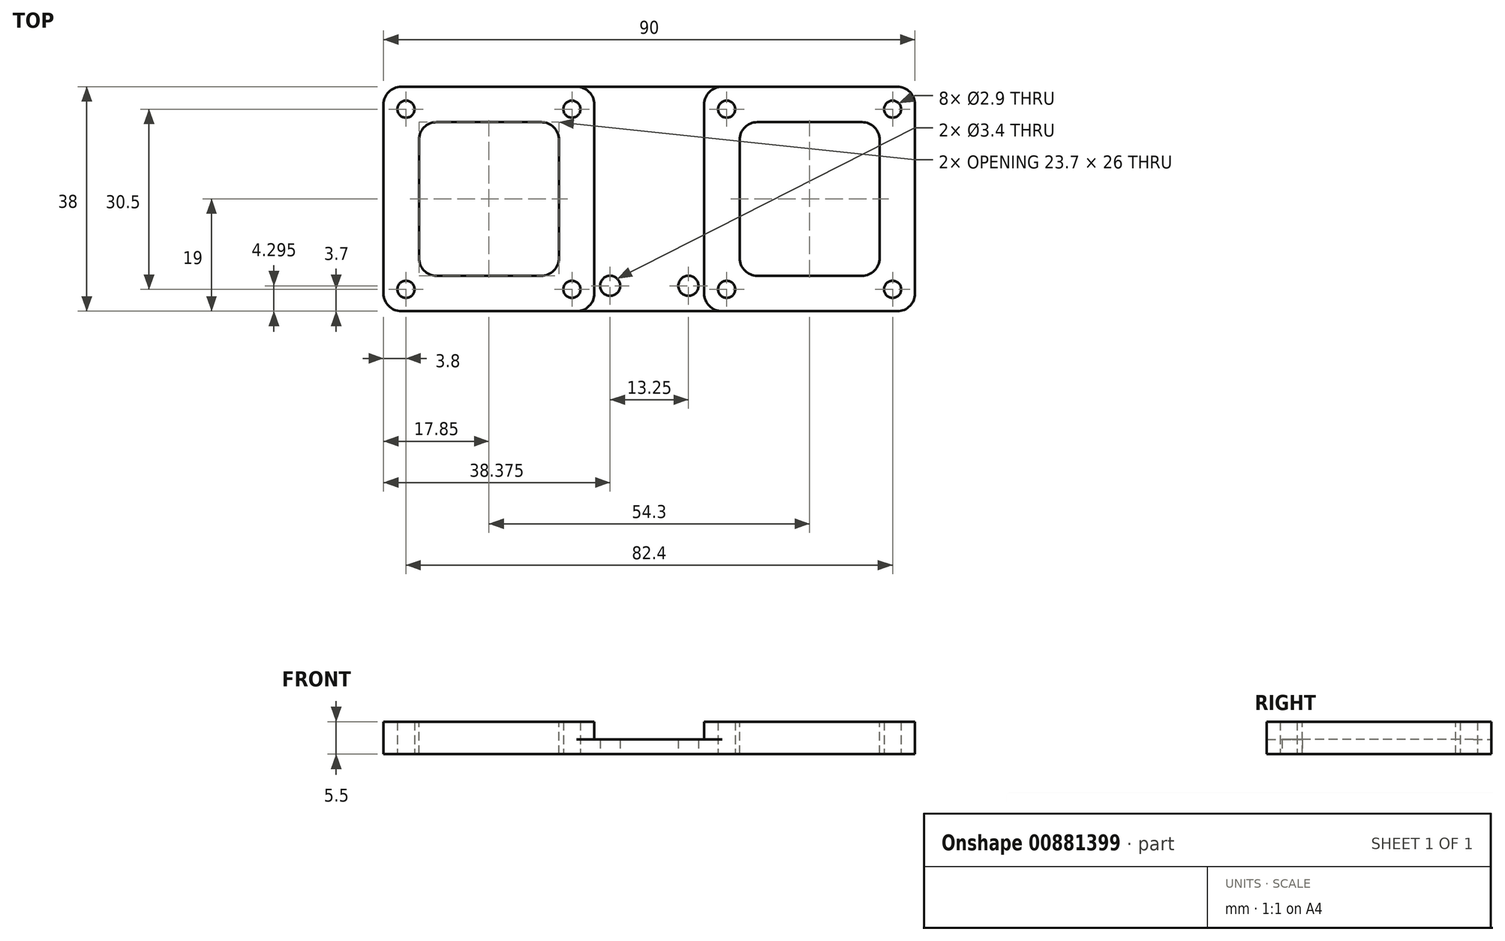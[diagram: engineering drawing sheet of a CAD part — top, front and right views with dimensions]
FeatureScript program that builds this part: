
annotation { "Feature Type Name" : "Feature", "Feature Type Description" : "" }
export const myFeature = defineFeature(function(context is Context, id is Id, definition is map)
    precondition{}
    {
        {
            var Q0;
            Q0=qCreatedBy(makeId("Top.planeOp"),FACE);
            var sketch = newSketch(context, id + "F0", { "sketchPlane" : qUnion([Q0])});
            skLineSegment(sketch, "E0.bottom", {"start": v(45, -19) * mm, "end": v(-45, -19) * mm});
            skLineSegment(sketch, "E0.top", {"start": v(45, 19) * mm, "end": v(-45, 19) * mm});
            skLineSegment(sketch, "E0.left", {"start": v(45, -19) * mm, "end": v(45, 19) * mm});
            skLineSegment(sketch, "E0.right", {"start": v(-45, -19) * mm, "end": v(-45, 19) * mm});
            skPoint(sketch, "E0.middle", {"position": v(0, 0) * mm});
            skSolve(sketch);
        }
        {
            var Q0;
            Q0=makeQuery(id+"F0.imprint","IMPRINT",FACE,{"disambiguationData":[TD([[makeQuery(id+"F0.imprint","IMPRINT",EDGE,{"derivedFrom":sQuery(id+"F0.wireOp",EDGE,"E0.bottom")}),-1.0]])]});
            extrude(context, id + "F1", {"entities" : qUnion([Q0]), "depth" : 2.5 * mm, "offsetDistance" : 25 * mm});
        }
        {
            var Q0;
            Q0=makeQuery(id+"F1.opExtrude","CAP_FACE",FACE,{"disambiguationData":[OSD([sQuery(id+"F0.wireOp",EDGE,"E0.bottom"),sQuery(id+"F0.wireOp",EDGE,"E0.top"),sQuery(id+"F0.wireOp",EDGE,"E0.left"),sQuery(id+"F0.wireOp",EDGE,"E0.right")])],"isStart":false});
            var sketch = newSketch(context, id + "F2", { "sketchPlane" : qUnion([Q0])});
            skPoint(sketch, "E1", {"position": v(-9.3, 19) * mm});
            skPoint(sketch, "E2", {"position": v(-9.3, -19) * mm});
            skPoint(sketch, "E3", {"position": v(9.3, 19) * mm});
            skPoint(sketch, "E4", {"position": v(9.3, -19) * mm});
            skLineSegment(sketch, "E5", {"start": v(-9.3, 19) * mm, "end": v(-9.3, -19) * mm});
            skLineSegment(sketch, "E6", {"start": v(9.3, 19) * mm, "end": v(9.3, -19) * mm});
            skPoint(sketch, "E7", {"position": v(6.62, -14.7) * mm});
            skPoint(sketch, "E8", {"position": v(-6.62, -14.7) * mm});
            skPoint(sketch, "E9", {"position": v(0, -14.7) * mm});
            skSolve(sketch);
        }
        {
            var Q0;
            Q0=sQuery(id+"F2.wireOp",VERTEX,"E7");
            var Q1;
            Q1=sQuery(id+"F2.wireOp",VERTEX,"E8");
            var Q2;
            Q2=makeQuery(id+"F1.opExtrude","SWEPT_BODY",BODY,{"disambiguationData":[OSD([sQuery(id+"F0.wireOp",EDGE,"E0.bottom"),sQuery(id+"F0.wireOp",EDGE,"E0.top"),sQuery(id+"F0.wireOp",EDGE,"E0.left"),sQuery(id+"F0.wireOp",EDGE,"E0.right")])]});
            hole(context, id + "F3", {"style" : HoleStyle.SIMPLE, "endStyle" : HoleEndStyle.THROUGH, "standardTappedOrClearance" : lookupTablePath({ "fit" : "Normal", "standard" : "ISO", "size" : "M3", "type" : "Clearance" }), "standardBlindInLast" : lookupTablePath({ "fit" : "Normal", "standard" : "ISO", "engagement" : "75%", "pitch" : "0.5 mm", "size" : "M3", "type" : "Clearance & tapped" }), "holeDiameter" : 3.4 * mm, "majorDiameter" : 5 * mm, "isTappedThrough" : true, "tappedDepth" : 12 * mm, "tapClearance" : 3, "locations" : qUnion([Q0, Q1]), "scope" : qUnion([Q2]), "startStyle" : HoleStartStyle.SKETCH});
        }
        {
            var Q0;
            {var subQ0=sQuery(id+"F2.wireOp",EDGE,"E5");Q0=makeQuery(id+"F2.imprint","IMPRINT",FACE,{"disambiguationData":[TD([[makeQuery(id+"F2.imprint","IMPRINT",EDGE,{"derivedFrom":subQ0}),-1.0]])]});}
            var Q1;
            {var subQ0=sQuery(id+"F2.wireOp",EDGE,"E6");Q1=makeQuery(id+"F2.imprint","IMPRINT",FACE,{"disambiguationData":[TD([[makeQuery(id+"F2.imprint","IMPRINT",EDGE,{"derivedFrom":subQ0}),1.0]])]});}
            extrude(context, id + "F4", {"entities" : qUnion([Q0, Q1]), "operationType" : NewBodyOperationType.ADD, "depth" : 3 * mm, "offsetDistance" : 25 * mm});
        }
        {
            var Q0;
            Q0=makeQuery(id+"F4.opExtrude","CAP_FACE",FACE,{"disambiguationData":[OSD([sQuery(id+"F0.wireOp",EDGE,"E0.bottom"),sQuery(id+"F0.wireOp",EDGE,"E0.top"),sQuery(id+"F0.wireOp",EDGE,"E0.right"),sQuery(id+"F2.wireOp",EDGE,"E5")])],"isStart":false});
            var sketch = newSketch(context, id + "F5", { "sketchPlane" : qUnion([Q0])});
            skLineSegment(sketch, "E10.0", {"start": v(39, 13) * mm, "end": v(15.3, 13) * mm});
            skLineSegment(sketch, "E10.1", {"start": v(39, -13) * mm, "end": v(39, 13) * mm});
            skLineSegment(sketch, "E10.2", {"start": v(15.3, -13) * mm, "end": v(39, -13) * mm});
            skLineSegment(sketch, "E10.3", {"start": v(15.3, 13) * mm, "end": v(15.3, -13) * mm});
            skSolve(sketch);
        }
        {
            var Q0;
            {var subQ0=sQuery(id+"F2.wireOp",EDGE,"E5");Q0=makeQuery(id+"F5.imprint","IMPRINT",FACE,{"disambiguationData":[TD([[makeQuery(id+"F5.imprint","IMPRINT",EDGE,{"derivedFrom":makeQuery(id+"F4.opExtrude","CAP_EDGE",EDGE,{"disambiguationData":[OSD([subQ0])],"isStart":false})}),-1.0]])]});}
            var sketch = newSketch(context, id + "F6", { "sketchPlane" : qUnion([Q0])});
            skLineSegment(sketch, "E11.0", {"start": v(-15.3, -13) * mm, "end": v(-15.3, 13) * mm});
            skLineSegment(sketch, "E11.1", {"start": v(-39, -13) * mm, "end": v(-15.3, -13) * mm});
            skLineSegment(sketch, "E11.2", {"start": v(-39, 13) * mm, "end": v(-39, -13) * mm});
            skLineSegment(sketch, "E11.3", {"start": v(-15.3, 13) * mm, "end": v(-39, 13) * mm});
            skSolve(sketch);
        }
        {
            var Q0;
            Q0=makeQuery(id+"F6.imprint","IMPRINT",FACE,{"disambiguationData":[TD([[makeQuery(id+"F6.imprint","IMPRINT",EDGE,{"derivedFrom":sQuery(id+"F6.wireOp",EDGE,"E11.0")}),1.0]])]});
            var Q1;
            Q1=makeQuery(id+"F5.imprint","IMPRINT",FACE,{"disambiguationData":[TD([[makeQuery(id+"F5.imprint","IMPRINT",EDGE,{"derivedFrom":sQuery(id+"F5.wireOp",EDGE,"E10.0")}),1.0]])]});
            extrude(context, id + "F7", {"entities" : qUnion([Q0, Q1]), "operationType" : NewBodyOperationType.REMOVE, "oppositeDirection" : true, "depth" : 10 * mm, "offsetDistance" : 25 * mm});
        }
        {
            var Q0;
            Q0=makeQuery(id+"F4.opExtrude","CAP_FACE",FACE,{"disambiguationData":[OSD([sQuery(id+"F0.wireOp",EDGE,"E0.bottom"),sQuery(id+"F0.wireOp",EDGE,"E0.top"),sQuery(id+"F0.wireOp",EDGE,"E0.right"),sQuery(id+"F2.wireOp",EDGE,"E5")])],"isStart":false});
            var sketch = newSketch(context, id + "F8", { "sketchPlane" : qUnion([Q0])});
            skPoint(sketch, "E12", {"position": v(-41.2, 15.2) * mm});
            skPoint(sketch, "E13", {"position": v(-13.1, 15.2) * mm});
            skPoint(sketch, "E14", {"position": v(-13.1, -15.3) * mm});
            skPoint(sketch, "E15", {"position": v(-41.2, -15.3) * mm});
            skSolve(sketch);
        }
        {
            var Q0;
            Q0=makeQuery(id+"F4.opExtrude","CAP_FACE",FACE,{"disambiguationData":[OSD([sQuery(id+"F0.wireOp",EDGE,"E0.bottom"),sQuery(id+"F0.wireOp",EDGE,"E0.top"),sQuery(id+"F0.wireOp",EDGE,"E0.left"),sQuery(id+"F2.wireOp",EDGE,"E6")])],"isStart":false});
            var sketch = newSketch(context, id + "F9", { "sketchPlane" : qUnion([Q0])});
            skPoint(sketch, "E16", {"position": v(13.1, 15.2) * mm});
            skPoint(sketch, "E17", {"position": v(41.2, 15.2) * mm});
            skPoint(sketch, "E18", {"position": v(13.1, -15.3) * mm});
            skPoint(sketch, "E19", {"position": v(41.2, -15.3) * mm});
            skSolve(sketch);
        }
        {
            var Q0;
            Q0=sQuery(id+"F8.wireOp",VERTEX,"E12");
            var Q1;
            Q1=sQuery(id+"F8.wireOp",VERTEX,"E15");
            var Q2;
            Q2=sQuery(id+"F8.wireOp",VERTEX,"E13");
            var Q3;
            Q3=sQuery(id+"F8.wireOp",VERTEX,"E14");
            var Q4;
            Q4=sQuery(id+"F9.wireOp",VERTEX,"E16");
            var Q5;
            Q5=sQuery(id+"F9.wireOp",VERTEX,"E17");
            var Q6;
            Q6=sQuery(id+"F9.wireOp",VERTEX,"E18");
            var Q7;
            Q7=sQuery(id+"F9.wireOp",VERTEX,"E19");
            var Q8;
            Q8=makeQuery(id+"F1.opExtrude","SWEPT_BODY",BODY,{"disambiguationData":[OSD([sQuery(id+"F0.wireOp",EDGE,"E0.bottom"),sQuery(id+"F0.wireOp",EDGE,"E0.top"),sQuery(id+"F0.wireOp",EDGE,"E0.left"),sQuery(id+"F0.wireOp",EDGE,"E0.right")])]});
            hole(context, id + "F10", {"style" : HoleStyle.SIMPLE, "endStyle" : HoleEndStyle.THROUGH, "standardTappedOrClearance" : lookupTablePath({ "fit" : "Normal", "standard" : "ISO", "size" : "M2.5", "type" : "Clearance" }), "standardBlindInLast" : lookupTablePath({ "fit" : "Normal", "standard" : "ISO", "engagement" : "75%", "pitch" : "0.35 mm", "size" : "M2.5", "type" : "Clearance & tapped" }), "holeDiameter" : 2.9 * mm, "majorDiameter" : 5 * mm, "isTappedThrough" : true, "tappedDepth" : 12 * mm, "tapClearance" : 3, "locations" : qUnion([Q0, Q1, Q2, Q3, Q4, Q5, Q6, Q7]), "scope" : qUnion([Q8]), "startStyle" : HoleStartStyle.SKETCH});
        }
        {
            var Q0;
            {var subQ0=sQuery(id+"F0.wireOp",EDGE,"E0.right");var subQ1=sQuery(id+"F0.wireOp",EDGE,"E0.top");Q0=makeQuery(id+"F4.boolean.opBoolean","MERGE",EDGE,{"derivedFrom":[makeQuery(id+"F1.opExtrude","SWEPT_EDGE",EDGE,{"disambiguationData":[OSD([subQ1,subQ0])]}),makeQuery(id+"F4.opExtrude","SWEPT_EDGE",EDGE,{"disambiguationData":[OSD([subQ1,subQ0])]})]});}
            var Q1;
            Q1=makeQuery(id+"F4.opExtrude","SWEPT_EDGE",EDGE,{"disambiguationData":[OSD([sQuery(id+"F0.wireOp",EDGE,"E0.top"),sQuery(id+"F2.wireOp",EDGE,"E6")])]});
            var Q2;
            {var subQ0=sQuery(id+"F0.wireOp",EDGE,"E0.left");var subQ1=sQuery(id+"F0.wireOp",EDGE,"E0.top");Q2=makeQuery(id+"F4.boolean.opBoolean","MERGE",EDGE,{"derivedFrom":[makeQuery(id+"F1.opExtrude","SWEPT_EDGE",EDGE,{"disambiguationData":[OSD([subQ1,subQ0])]}),makeQuery(id+"F4.opExtrude","SWEPT_EDGE",EDGE,{"disambiguationData":[OSD([subQ1,subQ0])]})]});}
            var Q3;
            Q3=makeQuery(id+"F7.boolean.opBoolean","COPY",EDGE,{"derivedFrom":makeQuery(id+"F7.opExtrude","SWEPT_EDGE",EDGE,{"disambiguationData":[OSD([sQuery(id+"F5.wireOp",EDGE,"E10.1"),sQuery(id+"F5.wireOp",EDGE,"E10.2")])]})});
            var Q4;
            Q4=makeQuery(id+"F7.boolean.opBoolean","COPY",EDGE,{"derivedFrom":makeQuery(id+"F7.opExtrude","SWEPT_EDGE",EDGE,{"disambiguationData":[OSD([sQuery(id+"F6.wireOp",EDGE,"E11.0"),sQuery(id+"F6.wireOp",EDGE,"E11.1")])]})});
            var Q5;
            {var subQ0=sQuery(id+"F0.wireOp",EDGE,"E0.right");var subQ1=sQuery(id+"F0.wireOp",EDGE,"E0.bottom");Q5=makeQuery(id+"F4.boolean.opBoolean","MERGE",EDGE,{"derivedFrom":[makeQuery(id+"F1.opExtrude","SWEPT_EDGE",EDGE,{"disambiguationData":[OSD([subQ1,subQ0])]}),makeQuery(id+"F4.opExtrude","SWEPT_EDGE",EDGE,{"disambiguationData":[OSD([subQ1,subQ0])]})]});}
            var Q6;
            Q6=makeQuery(id+"F4.opExtrude","SWEPT_EDGE",EDGE,{"disambiguationData":[OSD([sQuery(id+"F0.wireOp",EDGE,"E0.bottom"),sQuery(id+"F2.wireOp",EDGE,"E5")])]});
            var Q7;
            Q7=makeQuery(id+"F7.boolean.opBoolean","COPY",EDGE,{"derivedFrom":makeQuery(id+"F7.opExtrude","SWEPT_EDGE",EDGE,{"disambiguationData":[OSD([sQuery(id+"F6.wireOp",EDGE,"E11.2"),sQuery(id+"F6.wireOp",EDGE,"E11.3")])]})});
            var Q8;
            Q8=makeQuery(id+"F4.opExtrude","SWEPT_EDGE",EDGE,{"disambiguationData":[OSD([sQuery(id+"F0.wireOp",EDGE,"E0.top"),sQuery(id+"F2.wireOp",EDGE,"E5")])]});
            var Q9;
            Q9=makeQuery(id+"F7.boolean.opBoolean","COPY",EDGE,{"derivedFrom":makeQuery(id+"F7.opExtrude","SWEPT_EDGE",EDGE,{"disambiguationData":[OSD([sQuery(id+"F5.wireOp",EDGE,"E10.0"),sQuery(id+"F5.wireOp",EDGE,"E10.3")])]})});
            var Q10;
            {var subQ0=sQuery(id+"F0.wireOp",EDGE,"E0.left");var subQ1=sQuery(id+"F0.wireOp",EDGE,"E0.bottom");Q10=makeQuery(id+"F4.boolean.opBoolean","MERGE",EDGE,{"derivedFrom":[makeQuery(id+"F1.opExtrude","SWEPT_EDGE",EDGE,{"disambiguationData":[OSD([subQ1,subQ0])]}),makeQuery(id+"F4.opExtrude","SWEPT_EDGE",EDGE,{"disambiguationData":[OSD([subQ1,subQ0])]})]});}
            var Q11;
            Q11=makeQuery(id+"F7.boolean.opBoolean","COPY",EDGE,{"derivedFrom":makeQuery(id+"F7.opExtrude","SWEPT_EDGE",EDGE,{"disambiguationData":[OSD([sQuery(id+"F5.wireOp",EDGE,"E10.2"),sQuery(id+"F5.wireOp",EDGE,"E10.3")])]})});
            var Q12;
            Q12=makeQuery(id+"F7.boolean.opBoolean","COPY",EDGE,{"derivedFrom":makeQuery(id+"F7.opExtrude","SWEPT_EDGE",EDGE,{"disambiguationData":[OSD([sQuery(id+"F6.wireOp",EDGE,"E11.1"),sQuery(id+"F6.wireOp",EDGE,"E11.2")])]})});
            var Q13;
            Q13=makeQuery(id+"F7.boolean.opBoolean","COPY",EDGE,{"derivedFrom":makeQuery(id+"F7.opExtrude","SWEPT_EDGE",EDGE,{"disambiguationData":[OSD([sQuery(id+"F6.wireOp",EDGE,"E11.0"),sQuery(id+"F6.wireOp",EDGE,"E11.3")])]})});
            var Q14;
            Q14=makeQuery(id+"F7.boolean.opBoolean","COPY",EDGE,{"derivedFrom":makeQuery(id+"F7.opExtrude","SWEPT_EDGE",EDGE,{"disambiguationData":[OSD([sQuery(id+"F5.wireOp",EDGE,"E10.0"),sQuery(id+"F5.wireOp",EDGE,"E10.1")])]})});
            var Q15;
            Q15=makeQuery(id+"F4.opExtrude","SWEPT_EDGE",EDGE,{"disambiguationData":[OSD([sQuery(id+"F0.wireOp",EDGE,"E0.bottom"),sQuery(id+"F2.wireOp",EDGE,"E6")])]});
            fillet(context, id + "F11", {"entities" : qUnion([Q0, Q1, Q2, Q3, Q4, Q5, Q6, Q7, Q8, Q9, Q10, Q11, Q12, Q13, Q14, Q15]), "tangentPropagation" : true, "radius" : 3 * mm, "defaultsChanged" : false, "vertexSettings" : [], "allowEdgeOverflow" : false});
        }
    });
